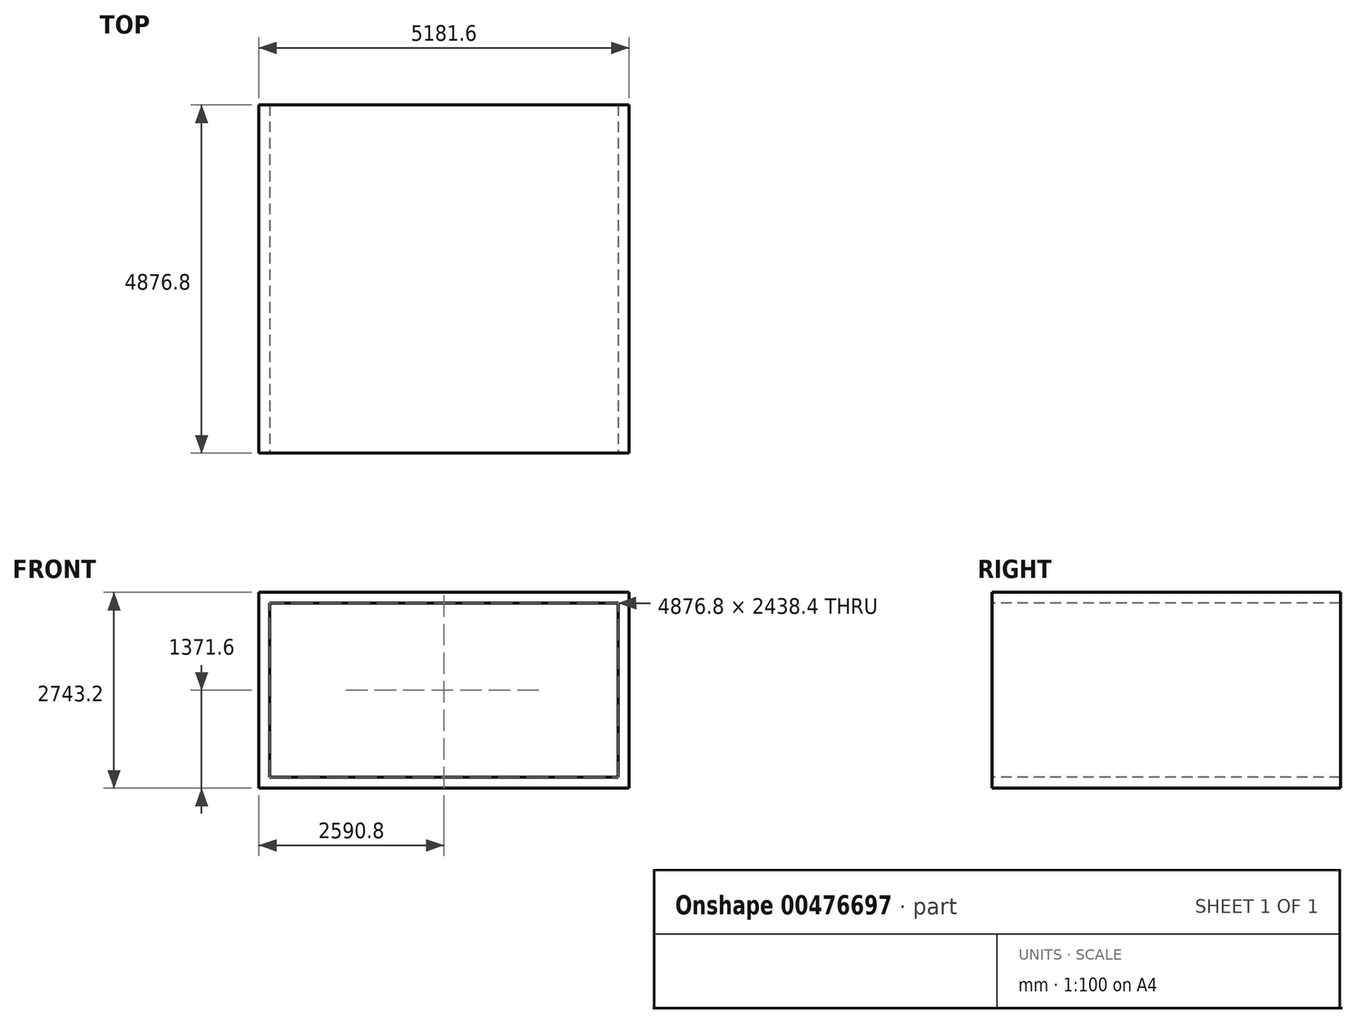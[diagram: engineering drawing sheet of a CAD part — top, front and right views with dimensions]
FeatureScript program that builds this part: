
annotation { "Feature Type Name" : "Feature", "Feature Type Description" : "" }
export const myFeature = defineFeature(function(context is Context, id is Id, definition is map)
    precondition{}
    {
        {
            var Q0;
            Q0=qCreatedBy(makeId("Front.planeOp"),FACE);
            var sketch = newSketch(context, id + "F0", { "sketchPlane" : qUnion([Q0])});
            skLineSegment(sketch, "E0.bottom", {"start": v(2438.4, -1219.2) * mm, "end": v(-2438.4, -1219.2) * mm});
            skLineSegment(sketch, "E0.top", {"start": v(2438.4, 1219.2) * mm, "end": v(-2438.4, 1219.2) * mm});
            skLineSegment(sketch, "E0.left", {"start": v(2438.4, -1219.2) * mm, "end": v(2438.4, 1219.2) * mm});
            skLineSegment(sketch, "E0.right", {"start": v(-2438.4, -1219.2) * mm, "end": v(-2438.4, 1219.2) * mm});
            skPoint(sketch, "E0.middle", {"position": v(0, 0) * mm});
            skLineSegment(sketch, "E1.0", {"start": v(2590.8, 1371.6) * mm, "end": v(-2590.8, 1371.6) * mm});
            skLineSegment(sketch, "E1.1", {"start": v(2590.8, -1371.6) * mm, "end": v(2590.8, 1371.6) * mm});
            skLineSegment(sketch, "E1.2", {"start": v(2590.8, -1371.6) * mm, "end": v(-2590.8, -1371.6) * mm});
            skLineSegment(sketch, "E1.3", {"start": v(-2590.8, -1371.6) * mm, "end": v(-2590.8, 1371.6) * mm});
            skSolve(sketch);
        }
        {
            var Q0;
            Q0 = qSketchRegion(id + "F0", true);
            extrude(context, id + "F1", {"entities" : qUnion([Q0]), "oppositeDirection" : true, "depth" : 4876.8 * mm});
        }
    });
